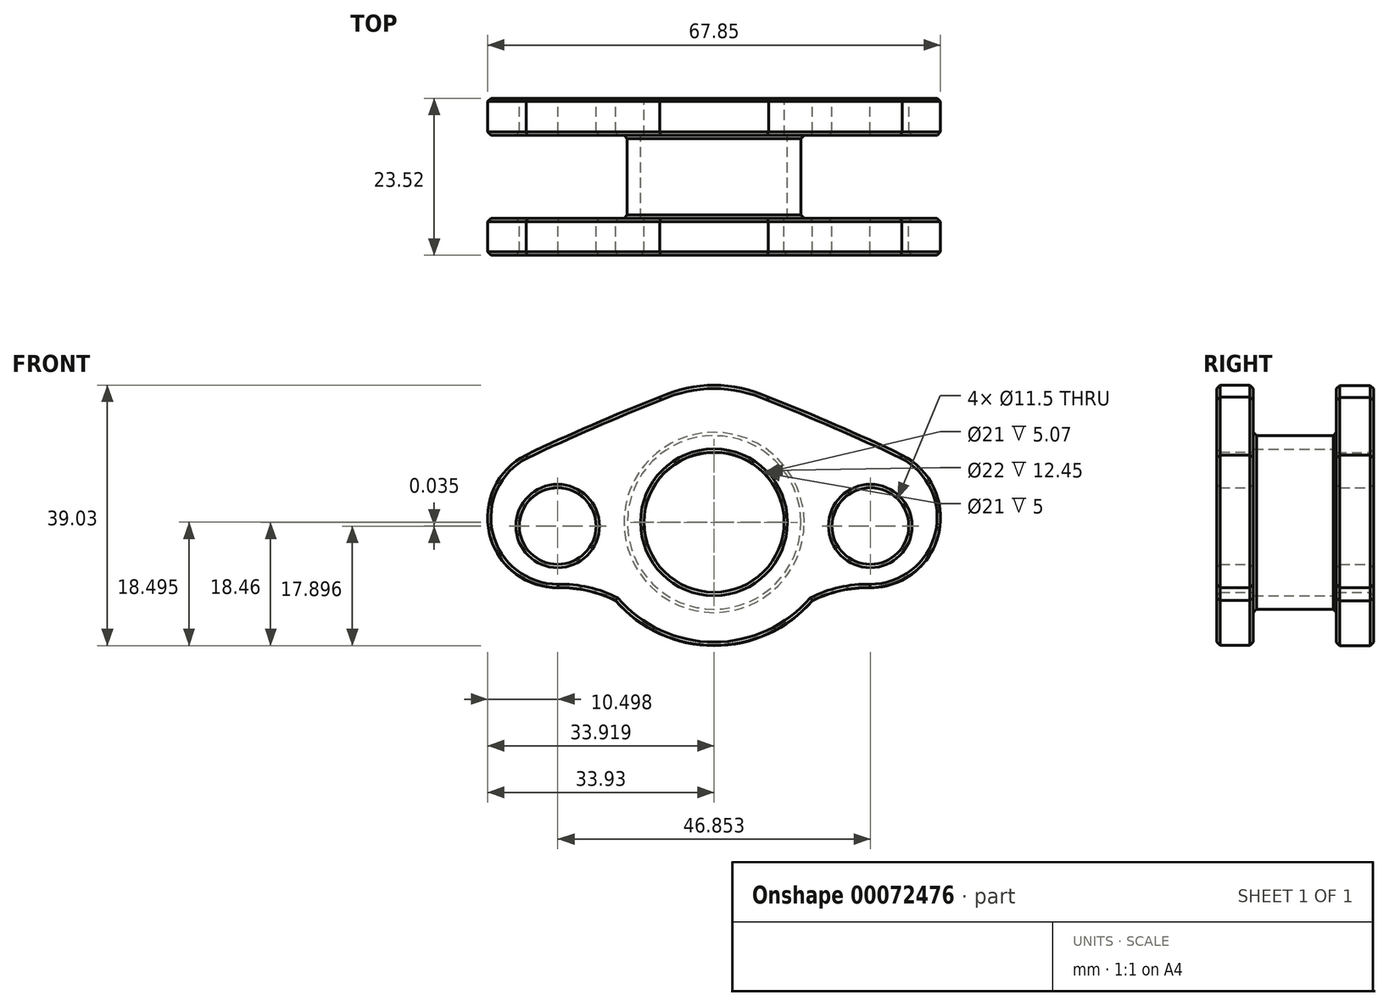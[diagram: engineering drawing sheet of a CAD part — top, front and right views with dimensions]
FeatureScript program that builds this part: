
annotation { "Feature Type Name" : "Feature", "Feature Type Description" : "" }
export const myFeature = defineFeature(function(context is Context, id is Id, definition is map)
    precondition{}
    {
        {
            var Q0;
            Q0=qCreatedBy(makeId("Front.planeOp"),FACE);
            var sketch = newSketch(context, id + "F0", { "sketchPlane" : qUnion([Q0])});
            skCircle(sketch, "E0", {"center": v(0, 0) * mm, "radius": 10.5 * mm});
            skCircle(sketch, "E1", {"center": v(-23.42, -0.56) * mm, "radius": 5.75 * mm});
            skCircle(sketch, "E2.MirrorC", {"center": v(23.42, -0.56) * mm, "radius": 5.75 * mm});
            skArc(sketch, "E3", {"start": v(-14.75, -11.72) * mm, "mid": v(-18.94, -10.24) * mm, "end": v(-23.36, -9.79) * mm});
            skArc(sketch, "E4", {"start": v(-8.15, 18.75) * mm, "mid": v(-18.23, 14.59) * mm, "end": v(-28.16, 10.08) * mm});
            skArc(sketch, "E5", {"start": v(-14.75, -11.72) * mm, "mid": v(0, -18.46) * mm, "end": v(14.75, -11.72) * mm});
            skArc(sketch, "E6", {"start": v(-28.16, 10.08) * mm, "mid": v(-33.61, -1.82) * mm, "end": v(-23.22, -9.79) * mm});
            skArc(sketch, "E7.MirrorCS", {"start": v(14.75, -11.72) * mm, "mid": v(18.94, -10.24) * mm, "end": v(23.36, -9.79) * mm});
            skArc(sketch, "E8.MirrorCS", {"start": v(28.16, 10.08) * mm, "mid": v(33.61, -1.82) * mm, "end": v(23.22, -9.79) * mm});
            skArc(sketch, "E9.MirrorCS", {"start": v(8.15, 18.75) * mm, "mid": v(18.23, 14.59) * mm, "end": v(28.16, 10.08) * mm});
            skArc(sketch, "E10", {"start": v(8.15, 18.75) * mm, "mid": v(0, 20.54) * mm, "end": v(-8.15, 18.75) * mm});
            skLineSegment(sketch, "E11", {"start": v(-23.42, -0.56) * mm, "end": v(0, 0) * mm, "construction": true});
            skLineSegment(sketch, "E12", {"start": v(0, 0) * mm, "end": v(0, 20.54) * mm, "construction": true});
            skLineSegment(sketch, "E13", {"start": v(-23.42, -0.56) * mm, "end": v(-23.73, 12.14) * mm, "construction": true});
            skLineSegment(sketch, "E14", {"start": v(-23.42, -0.56) * mm, "end": v(-33.84, -0.56) * mm, "construction": true});
            skSolve(sketch);
        }
        {
            var Q0;
            Q0=makeQuery(id+"F0.imprint","IMPRINT",FACE,{"disambiguationData":[TD([[makeQuery(id+"F0.imprint","IMPRINT",EDGE,{"derivedFrom":sQuery(id+"F0.wireOp",EDGE,"E0")}),-1.0]])]});
            extrude(context, id + "F1", {"entities" : qUnion([Q0]), "depth" : 5.57 * mm});
        }
        {
            var Q0;
            Q0=makeQuery(id+"F1.opExtrude","CAP_FACE",FACE,{"disambiguationData":[OSD([sQuery(id+"F0.wireOp",EDGE,"E0"),sQuery(id+"F0.wireOp",EDGE,"E1"),sQuery(id+"F0.wireOp",EDGE,"E2.MirrorC"),sQuery(id+"F0.wireOp",EDGE,"E3"),sQuery(id+"F0.wireOp",EDGE,"E4"),sQuery(id+"F0.wireOp",EDGE,"E5"),sQuery(id+"F0.wireOp",EDGE,"E6"),sQuery(id+"F0.wireOp",EDGE,"E7.MirrorCS"),sQuery(id+"F0.wireOp",EDGE,"E8.MirrorCS"),sQuery(id+"F0.wireOp",EDGE,"E9.MirrorCS"),sQuery(id+"F0.wireOp",EDGE,"E10")])],"isStart":false});
            var sketch = newSketch(context, id + "F2", { "sketchPlane" : qUnion([Q0])});
            skCircle(sketch, "E15", {"center": v(0, 0) * mm, "radius": 11 * mm});
            skCircle(sketch, "E16", {"center": v(0, 0) * mm, "radius": 13 * mm});
            skSolve(sketch);
        }
        {
            var Q0;
            Q0=makeQuery(id+"F2.imprint","IMPRINT",FACE,{"disambiguationData":[TD([[makeQuery(id+"F2.imprint","IMPRINT",EDGE,{"derivedFrom":sQuery(id+"F2.wireOp",EDGE,"E15")}),-1.0]])]});
            extrude(context, id + "F3", {"entities" : qUnion([Q0]), "operationType" : NewBodyOperationType.ADD, "depth" : 12.45 * mm});
        }
        {
            var Q0;
            Q0=makeQuery(id+"F3.opExtrude","CAP_FACE",FACE,{"disambiguationData":[OSD([sQuery(id+"F2.wireOp",EDGE,"E15"),sQuery(id+"F2.wireOp",EDGE,"E16")])],"isStart":false});
            var sketch = newSketch(context, id + "F4", { "sketchPlane" : qUnion([Q0])});
            skCircle(sketch, "E17", {"center": v(-0.01, 0.04) * mm, "radius": 10.5 * mm});
            skCircle(sketch, "E18", {"center": v(-23.43, -0.53) * mm, "radius": 5.75 * mm});
            skCircle(sketch, "E19.MirrorC", {"center": v(23.41, -0.53) * mm, "radius": 5.75 * mm});
            skArc(sketch, "E20", {"start": v(-14.76, -11.68) * mm, "mid": v(-18.95, -10.2) * mm, "end": v(-23.37, -9.75) * mm});
            skArc(sketch, "E21", {"start": v(-8.16, 18.79) * mm, "mid": v(-18.24, 14.62) * mm, "end": v(-28.17, 10.12) * mm});
            skArc(sketch, "E22", {"start": v(-14.76, -11.68) * mm, "mid": v(-0.01, -18.43) * mm, "end": v(14.74, -11.68) * mm});
            skArc(sketch, "E23", {"start": v(-28.17, 10.12) * mm, "mid": v(-33.62, -1.79) * mm, "end": v(-23.23, -9.75) * mm});
            skArc(sketch, "E24.MirrorCS", {"start": v(14.74, -11.68) * mm, "mid": v(18.93, -10.2) * mm, "end": v(23.34, -9.75) * mm});
            skArc(sketch, "E25.MirrorCS", {"start": v(28.14, 10.12) * mm, "mid": v(33.6, -1.79) * mm, "end": v(23.2, -9.75) * mm});
            skArc(sketch, "E26.MirrorCS", {"start": v(8.14, 18.79) * mm, "mid": v(18.22, 14.62) * mm, "end": v(28.14, 10.12) * mm});
            skArc(sketch, "E27", {"start": v(8.14, 18.79) * mm, "mid": v(-0.01, 20.57) * mm, "end": v(-8.16, 18.79) * mm});
            skLineSegment(sketch, "E28", {"start": v(-23.43, -0.53) * mm, "end": v(-0.01, 0.04) * mm, "construction": true});
            skLineSegment(sketch, "E29", {"start": v(-0.01, 0.04) * mm, "end": v(-0.01, 20.57) * mm, "construction": true});
            skLineSegment(sketch, "E30", {"start": v(-23.43, -0.53) * mm, "end": v(-23.74, 12.18) * mm, "construction": true});
            skLineSegment(sketch, "E31", {"start": v(-23.43, -0.53) * mm, "end": v(-33.85, -0.53) * mm, "construction": true});
            skSolve(sketch);
        }
        {
            var Q0;
            {var subQ0=sQuery(id+"F4.wireOp",EDGE,"E23");var subQ1=sQuery(id+"F4.wireOp",EDGE,"E20");var subQ2=makeQuery(id+"F4.imprint","INTERSECT",VERTEX,{"disambiguationData":[OD(0.0)],"derivedFrom":[subQ1,subQ0]});Q0=makeQuery(id+"F4.imprint","IMPRINT",FACE,{"disambiguationData":[TD([[makeQuery(id+"F4.imprint","IMPRINT",EDGE,{"disambiguationData":[TD([[subQ2,-1.0]])],"derivedFrom":subQ1}),1.0]])]});}
            var Q1;
            {var subQ0=sQuery(id+"F4.wireOp",EDGE,"E25.MirrorCS");var subQ1=sQuery(id+"F4.wireOp",EDGE,"E24.MirrorCS");var subQ2=makeQuery(id+"F4.imprint","INTERSECT",VERTEX,{"disambiguationData":[OD(0.0)],"derivedFrom":[subQ1,subQ0]});Q1=makeQuery(id+"F4.imprint","IMPRINT",FACE,{"disambiguationData":[TD([[makeQuery(id+"F4.imprint","IMPRINT",EDGE,{"disambiguationData":[TD([[subQ2,1.0]])],"derivedFrom":subQ1}),-1.0]])]});}
            var Q2;
            Q2=makeQuery(id+"F4.imprint","IMPRINT",FACE,{"disambiguationData":[TD([[makeQuery(id+"F4.imprint","IMPRINT",EDGE,{"derivedFrom":sQuery(id+"F4.wireOp",EDGE,"E17")}),-1.0]])]});
            var Q3;
            Q3=makeQuery(id+"F4.imprint","IMPRINT",FACE,{"disambiguationData":[TD([[makeQuery(id+"F4.imprint","IMPRINT",EDGE,{"derivedFrom":makeQuery(id+"F3.opExtrude","CAP_EDGE",EDGE,{"disambiguationData":[OSD([sQuery(id+"F2.wireOp",EDGE,"E15")])],"isStart":false})}),-1.0]])]});
            var Q4;
            Q4=makeQuery(id+"F4.imprint","IMPRINT",FACE,{"disambiguationData":[TD([[makeQuery(id+"F4.imprint","IMPRINT",EDGE,{"derivedFrom":sQuery(id+"F4.wireOp",EDGE,"E18")}),-1.0]])]});
            extrude(context, id + "F5", {"entities" : qUnion([Q0, Q1, Q2, Q3, Q4]), "operationType" : NewBodyOperationType.ADD, "depth" : 5.5 * mm});
        }
        {
            var Q0;
            Q0=makeQuery(id+"F1.opExtrude","CAP_FACE",FACE,{"disambiguationData":[OSD([sQuery(id+"F0.wireOp",EDGE,"E0"),sQuery(id+"F0.wireOp",EDGE,"E1"),sQuery(id+"F0.wireOp",EDGE,"E2.MirrorC"),sQuery(id+"F0.wireOp",EDGE,"E3"),sQuery(id+"F0.wireOp",EDGE,"E4"),sQuery(id+"F0.wireOp",EDGE,"E5"),sQuery(id+"F0.wireOp",EDGE,"E6"),sQuery(id+"F0.wireOp",EDGE,"E7.MirrorCS"),sQuery(id+"F0.wireOp",EDGE,"E8.MirrorCS"),sQuery(id+"F0.wireOp",EDGE,"E9.MirrorCS"),sQuery(id+"F0.wireOp",EDGE,"E10")])],"isStart":true});
            var Q1;
            {var subQ0=sQuery(id+"F4.wireOp",EDGE,"E26.MirrorCS");var subQ1=sQuery(id+"F4.wireOp",EDGE,"E25.MirrorCS");var subQ2=sQuery(id+"F4.wireOp",EDGE,"E23");var subQ3=sQuery(id+"F4.wireOp",EDGE,"E22");var subQ4=sQuery(id+"F4.wireOp",EDGE,"E24.MirrorCS");var subQ5=sQuery(id+"F4.wireOp",EDGE,"E21");var subQ6=sQuery(id+"F4.wireOp",EDGE,"E18");var subQ7=sQuery(id+"F4.wireOp",EDGE,"E27");var subQ8=sQuery(id+"F4.wireOp",EDGE,"E19.MirrorC");var subQ9=sQuery(id+"F4.wireOp",EDGE,"E20");Q1=makeQuery(id+"F5.boolean.opBoolean","SPLIT",FACE,{"disambiguationData":[TD([makeQuery(id+"F3.opExtrude","SWEPT_FACE",FACE,{"disambiguationData":[OSD([sQuery(id+"F2.wireOp",EDGE,"E16")])]})])],"derivedFrom":makeQuery(id+"F5.opExtrude","CAP_FACE",FACE,{"disambiguationData":[OSD([sQuery(id+"F4.wireOp",EDGE,"E17"),subQ6,subQ8,subQ9,subQ5,subQ3,subQ2,subQ4,subQ1,subQ0,subQ7])],"isStart":true})});}
            var Q2;
            {var subQ0=sQuery(id+"F0.wireOp",EDGE,"E9.MirrorCS");var subQ1=sQuery(id+"F0.wireOp",EDGE,"E7.MirrorCS");var subQ2=sQuery(id+"F0.wireOp",EDGE,"E6");var subQ3=sQuery(id+"F0.wireOp",EDGE,"E5");var subQ4=sQuery(id+"F0.wireOp",EDGE,"E8.MirrorCS");var subQ5=sQuery(id+"F0.wireOp",EDGE,"E1");var subQ6=sQuery(id+"F0.wireOp",EDGE,"E2.MirrorC");var subQ7=sQuery(id+"F0.wireOp",EDGE,"E10");var subQ8=sQuery(id+"F0.wireOp",EDGE,"E3");var subQ9=sQuery(id+"F0.wireOp",EDGE,"E4");Q2=makeQuery(id+"F3.boolean.opBoolean","SPLIT",FACE,{"disambiguationData":[TD([makeQuery(id+"F1.opExtrude","SWEPT_FACE",FACE,{"disambiguationData":[OSD([subQ5])]})])],"derivedFrom":makeQuery(id+"F1.opExtrude","CAP_FACE",FACE,{"disambiguationData":[OSD([sQuery(id+"F0.wireOp",EDGE,"E0"),subQ5,subQ6,subQ8,subQ9,subQ3,subQ2,subQ1,subQ4,subQ0,subQ7])],"isStart":false})});}
            var Q3;
            Q3=makeQuery(id+"F5.opExtrude","CAP_FACE",FACE,{"disambiguationData":[OSD([sQuery(id+"F4.wireOp",EDGE,"E17"),sQuery(id+"F4.wireOp",EDGE,"E18"),sQuery(id+"F4.wireOp",EDGE,"E19.MirrorC"),sQuery(id+"F4.wireOp",EDGE,"E20"),sQuery(id+"F4.wireOp",EDGE,"E21"),sQuery(id+"F4.wireOp",EDGE,"E22"),sQuery(id+"F4.wireOp",EDGE,"E23"),sQuery(id+"F4.wireOp",EDGE,"E24.MirrorCS"),sQuery(id+"F4.wireOp",EDGE,"E25.MirrorCS"),sQuery(id+"F4.wireOp",EDGE,"E26.MirrorCS"),sQuery(id+"F4.wireOp",EDGE,"E27")])],"isStart":false});
            chamfer(context, id + "F6", {"entities" : qUnion([Q0, Q1, Q2, Q3]), "width" : .5 * mm, "tangentPropagation" : true});
        }
    });
